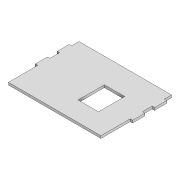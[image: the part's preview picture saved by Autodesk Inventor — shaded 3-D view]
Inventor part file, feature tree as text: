
AUTODESK INVENTOR PART (.ipt)
format: ipt  version: 2022 (Build 260153000, 153)  size: 124,416 bytes
history: native  units: mm
features: extrude x2, sketch x2, projected_geometry x1
ambient origin geometry x8: Origin, YZ Plane, XZ Plane, XY Plane, X Axis, Y Axis, Z Axis, Center Point
bodies: Solid1 (feature_tree)
feature tree (5):
  extrude  "Extrusion1"  Depth=145.0mm
  extrude  "Extrusion2"  Depth=25.0mm
  sketch  "Sketch1"  dims[d0=190.0mm d1=145.0mm]
  sketch  "Sketch2"  dims[d2=5.0mm d3=25.0mm d4=5.0mm d5=25.0mm d6=20.0mm d7=15.0mm d8=5.0mm d9=0.0mm d10=42.0mm d11=54.0mm d12=45.0mm d13=40.0mm d14=5.0mm d15=0.0mm]
  projected_geometry  "Projected Loop1"
